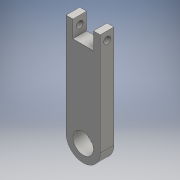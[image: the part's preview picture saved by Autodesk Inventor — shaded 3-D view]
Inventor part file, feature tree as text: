
AUTODESK INVENTOR PART (.ipt)
format: ipt  version: 2016 (Build 200138000, 138)  size: 124,416 bytes
history: native  units: mm
features: extrude x4, sketch x4, other x1
ambient origin geometry x8: Origin, YZ Plane, XZ Plane, XY Plane, X Axis, Y Axis, Z Axis, Center Point
bodies: Body1 (feature_tree)
feature tree (9):
  other  "ソリッド1"
  extrude  "押し出し1"  Depth=10.0mm
  extrude  "押し出し2"  Depth=35.0mm
  extrude  "押し出し3"  Depth=4.0mm TaperAngle=0.0deg
  extrude  "押し出し4"  Depth=6.0mm
  sketch  "スケッチ1"
  sketch  "スケッチ2"
  sketch  "スケッチ3"
  sketch  "スケッチ4"
